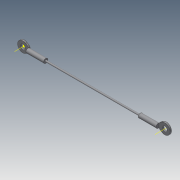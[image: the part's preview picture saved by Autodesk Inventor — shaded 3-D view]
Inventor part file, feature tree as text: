
AUTODESK INVENTOR PART (.ipt)
format: ipt  version: 2020.4 (Build 244396000, 396)  size: 141,824 bytes
history: native  units: in
note: dims shown in document units (in); Inventor stores cm internally (conversion verified against a paired STEP export)
features: sketch x4, extrude x3, plane x2, other x2, fillet x1, mirror x1
ambient origin geometry x8: Origin, YZ Plane, XZ Plane, XY Plane, X Axis, Y Axis, Z Axis, Center Point
bodies: Solid1 (feature_tree)
feature tree (13):
  extrude  "Extrusion1"  Depth=0.12in
  sketch  "Sketch2"  dims[d2=0.0625in d3=0.0in d4=1.0in d5=0.06in]
  plane  "Work Plane1"
  extrude  "Extrusion2"  Depth=1.0in
  fillet  "Fillet1"  Radius=0.06in
  sketch  "Sketch4"  dims[d9=0.2in d10=0.1in d11=0.07in d12=3.0in d13=1.0in d14=0.0in]
  plane  "Work Plane2"
  extrude  "Extrusion3"  Depth=0.25in
  mirror  "Mirror1"
  other  "Work Axis1"
  other  "Work Axis2"
  sketch  "Sketch1"  dims[d0=0.2031in d1=0.12in]
  sketch  "Sketch3"  dims[d6=0.75in d7=0.0in d8=0.25in]
